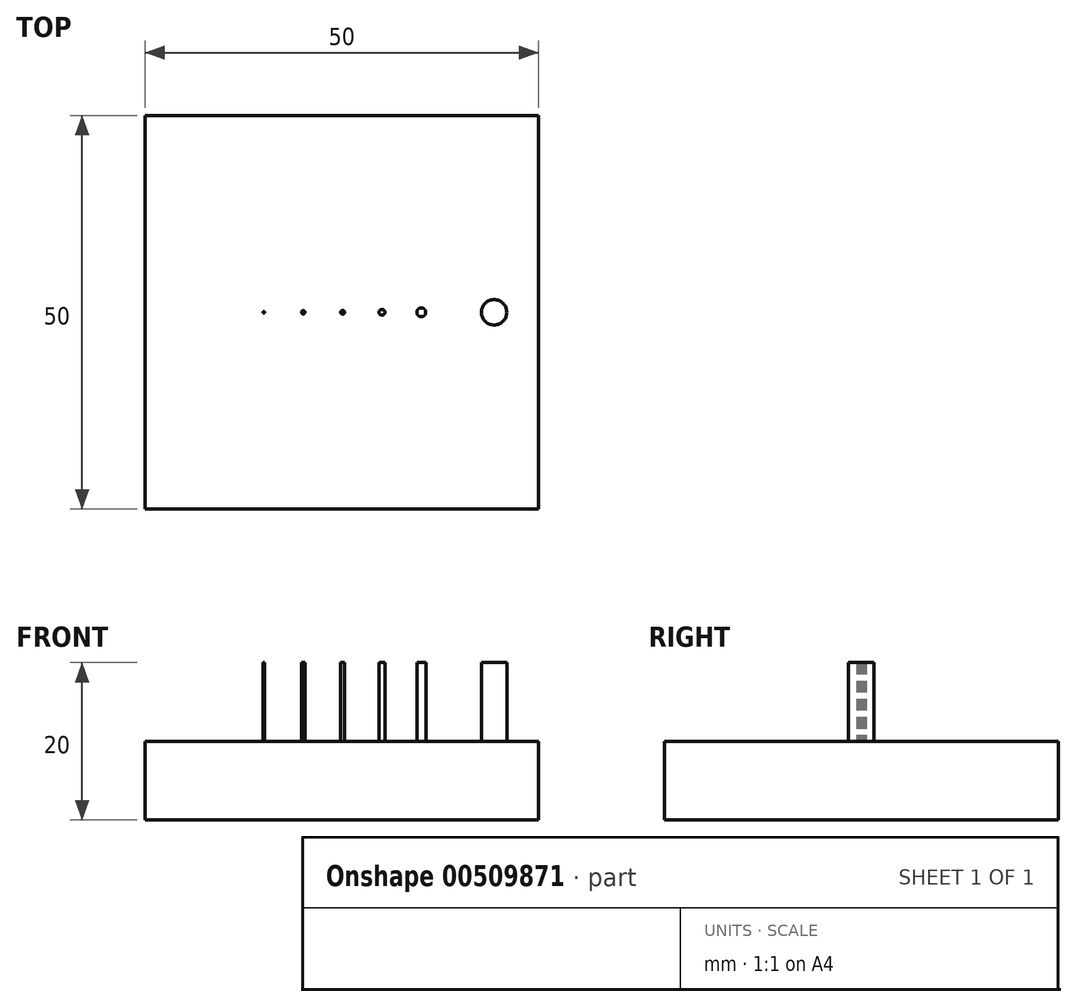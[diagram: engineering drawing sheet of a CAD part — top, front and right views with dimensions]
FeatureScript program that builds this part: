
annotation { "Feature Type Name" : "Feature", "Feature Type Description" : "" }
export const myFeature = defineFeature(function(context is Context, id is Id, definition is map)
    precondition{}
    {
        {
            var Q0;
            Q0=qCreatedBy(makeId("Top.planeOp"),FACE);
            var sketch = newSketch(context, id + "F0", { "sketchPlane" : qUnion([Q0])});
            skLineSegment(sketch, "E0.bottom", {"start": v(25, 25) * mm, "end": v(-25, 25) * mm});
            skLineSegment(sketch, "E0.top", {"start": v(25, -25) * mm, "end": v(-25, -25) * mm});
            skLineSegment(sketch, "E0.left", {"start": v(25, 25) * mm, "end": v(25, -25) * mm});
            skLineSegment(sketch, "E0.right", {"start": v(-25, 25) * mm, "end": v(-25, -25) * mm});
            skPoint(sketch, "E0.middle", {"position": v(0, 0) * mm});
            skSolve(sketch);
        }
        {
            var Q0;
            Q0=makeQuery(id+"F0.imprint","IMPRINT",FACE,{"disambiguationData":[TD([[makeQuery(id+"F0.imprint","IMPRINT",EDGE,{"derivedFrom":sQuery(id+"F0.wireOp",EDGE,"E0.bottom")}),1.0]])]});
            extrude(context, id + "F1", {"entities" : qUnion([Q0]), "depth" : 10 * mm});
        }
        {
            var Q0;
            Q0=makeQuery(id+"F1.opExtrude","CAP_FACE",FACE,{"disambiguationData":[OSD([sQuery(id+"F0.wireOp",EDGE,"E0.bottom"),sQuery(id+"F0.wireOp",EDGE,"E0.top"),sQuery(id+"F0.wireOp",EDGE,"E0.left"),sQuery(id+"F0.wireOp",EDGE,"E0.right")])],"isStart":false});
            var sketch = newSketch(context, id + "F2", { "sketchPlane" : qUnion([Q0])});
            skCircle(sketch, "E1", {"center": v(-9.9, 0) * mm, "radius": 0.1 * mm});
            skCircle(sketch, "E2", {"center": v(-4.9, 0) * mm, "radius": 0.22 * mm});
            skCircle(sketch, "E3", {"center": v(0.1, 0) * mm, "radius": 0.25 * mm});
            skCircle(sketch, "E4", {"center": v(5.1, 0) * mm, "radius": 0.38 * mm});
            skCircle(sketch, "E5", {"center": v(10.1, 0) * mm, "radius": 0.57 * mm});
            skCircle(sketch, "E6", {"center": v(19.35, 0) * mm, "radius": 1.61 * mm});
            skSolve(sketch);
        }
        {
            var Q0;
            Q0=makeQuery(id+"F2.imprint","IMPRINT",FACE,{"disambiguationData":[TD([[makeQuery(id+"F2.imprint","IMPRINT",EDGE,{"derivedFrom":sQuery(id+"F2.wireOp",EDGE,"E6")}),1.0]])]});
            var Q1;
            Q1=makeQuery(id+"F2.imprint","IMPRINT",FACE,{"disambiguationData":[TD([[makeQuery(id+"F2.imprint","IMPRINT",EDGE,{"derivedFrom":sQuery(id+"F2.wireOp",EDGE,"E5")}),1.0]])]});
            var Q2;
            Q2=makeQuery(id+"F2.imprint","IMPRINT",FACE,{"disambiguationData":[TD([[makeQuery(id+"F2.imprint","IMPRINT",EDGE,{"derivedFrom":sQuery(id+"F2.wireOp",EDGE,"E4")}),1.0]])]});
            var Q3;
            Q3=makeQuery(id+"F2.imprint","IMPRINT",FACE,{"disambiguationData":[TD([[makeQuery(id+"F2.imprint","IMPRINT",EDGE,{"derivedFrom":sQuery(id+"F2.wireOp",EDGE,"E3")}),1.0]])]});
            var Q4;
            Q4=makeQuery(id+"F2.imprint","IMPRINT",FACE,{"disambiguationData":[TD([[makeQuery(id+"F2.imprint","IMPRINT",EDGE,{"derivedFrom":sQuery(id+"F2.wireOp",EDGE,"E2")}),1.0]])]});
            var Q5;
            Q5=makeQuery(id+"F2.imprint","IMPRINT",FACE,{"disambiguationData":[TD([[makeQuery(id+"F2.imprint","IMPRINT",EDGE,{"derivedFrom":sQuery(id+"F2.wireOp",EDGE,"E1")}),1.0]])]});
            extrude(context, id + "F3", {"entities" : qUnion([Q0, Q1, Q2, Q3, Q4, Q5]), "operationType" : NewBodyOperationType.ADD, "depth" : 10 * mm});
        }
    });
